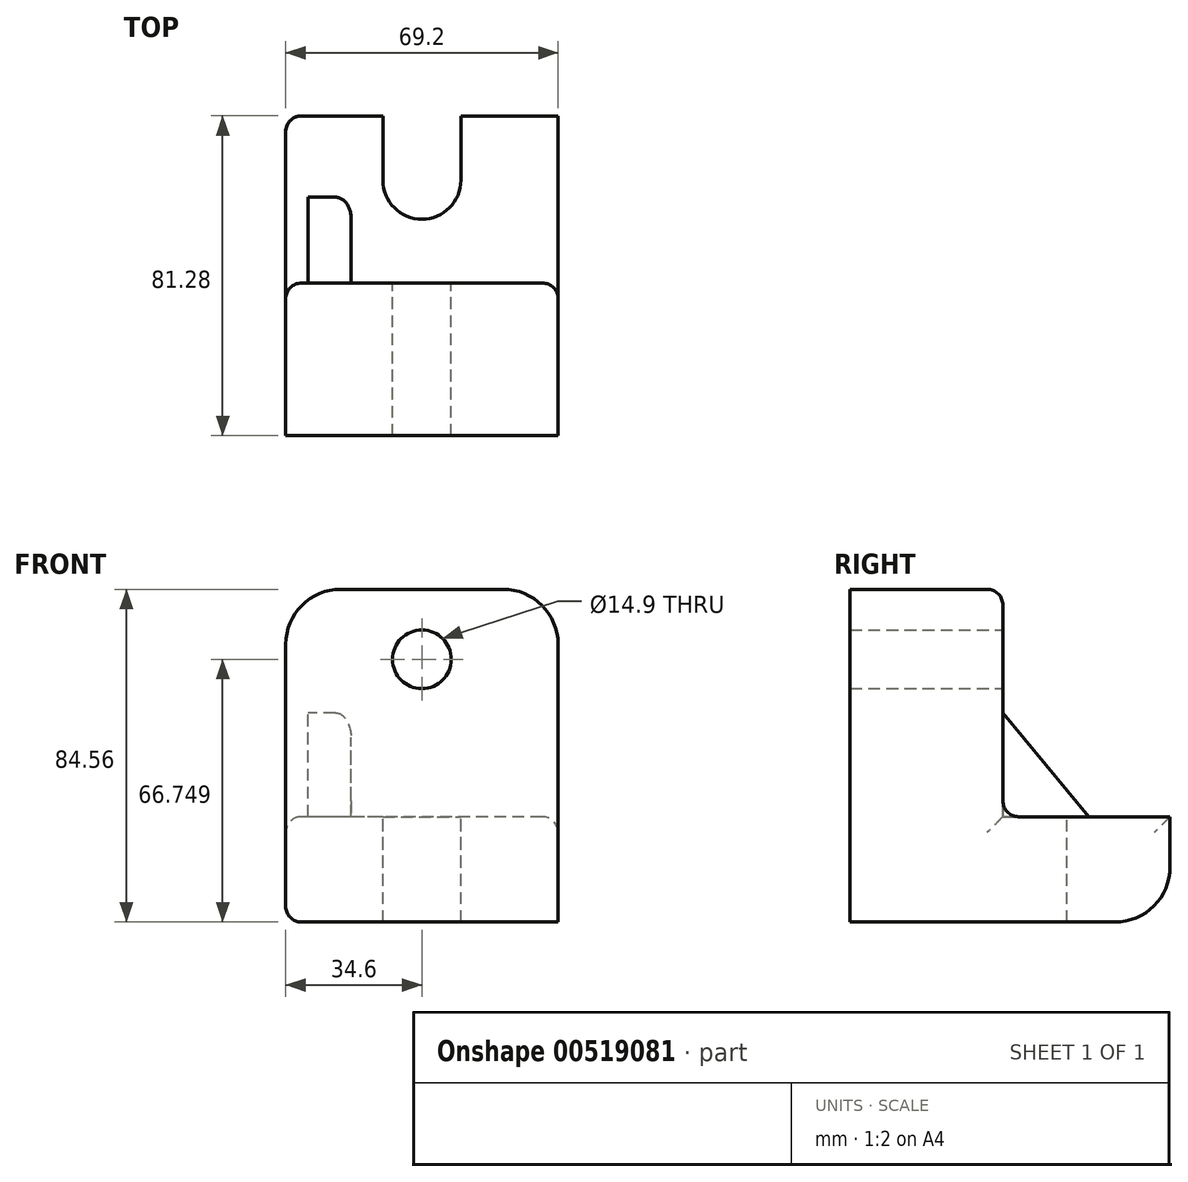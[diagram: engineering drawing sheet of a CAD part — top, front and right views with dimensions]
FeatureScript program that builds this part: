
annotation { "Feature Type Name" : "Feature", "Feature Type Description" : "" }
export const myFeature = defineFeature(function(context is Context, id is Id, definition is map)
    precondition{}
    {
        {
            var Q0;
            Q0=qCreatedBy(makeId("Right.planeOp"),FACE);
            var sketch = newSketch(context, id + "F0", { "sketchPlane" : qUnion([Q0])});
            skLineSegment(sketch, "E0.bottom", {"start": v(-19.4, 42.28) * mm, "end": v(19.4, 42.28) * mm});
            skLineSegment(sketch, "E0.top", {"start": v(-19.4, -42.28) * mm, "end": v(19.4, -42.28) * mm});
            skLineSegment(sketch, "E0.left", {"start": v(-19.4, 42.28) * mm, "end": v(-19.4, -42.28) * mm});
            skLineSegment(sketch, "E0.right", {"start": v(19.4, 42.28) * mm, "end": v(19.4, -15.52) * mm});
            skPoint(sketch, "E0.middle", {"position": v(0, 0) * mm});
            skLineSegment(sketch, "E1.bottom", {"start": v(-19.4, -42.28) * mm, "end": v(61.88, -42.28) * mm});
            skLineSegment(sketch, "E1.top", {"start": v(19.4, -15.52) * mm, "end": v(61.88, -15.52) * mm});
            skLineSegment(sketch, "E1.left", {"start": v(-19.4, -42.28) * mm, "end": v(-19.4, -15.52) * mm});
            skLineSegment(sketch, "E1.right", {"start": v(61.88, -42.28) * mm, "end": v(61.88, -15.52) * mm});
            skSolve(sketch);
        }
        {
            var Q0;
            Q0=makeQuery(id+"F0.imprint","IMPRINT",FACE,{"disambiguationData":[TD([[makeQuery(id+"F0.imprint","IMPRINT",EDGE,{"derivedFrom":sQuery(id+"F0.wireOp",EDGE,"E0.bottom")}),-1.0]])]});
            extrude(context, id + "F1", {"entities" : qUnion([Q0]), "endBound" : BoundingType.SYMMETRIC, "depth" : 69.2 * mm, "offsetDistance" : 25 * mm});
        }
        {
            var Q0;
            Q0=makeQuery(id+"F1.opExtrude","SWEPT_FACE",FACE,{"disambiguationData":[OSD([sQuery(id+"F0.wireOp",EDGE,"E1.top")])]});
            var sketch = newSketch(context, id + "F2", { "sketchPlane" : qUnion([Q0])});
            skCircle(sketch, "E2", {"center": v(0, 45.53) * mm, "radius": 9.91 * mm});
            skLineSegment(sketch, "E3", {"start": v(9.91, 45.53) * mm, "end": v(9.91, 61.88) * mm});
            skLineSegment(sketch, "E4", {"start": v(-9.91, 45.53) * mm, "end": v(-9.91, 61.88) * mm});
            skLineSegment(sketch, "E5", {"start": v(9.91, 61.88) * mm, "end": v(-9.91, 61.88) * mm});
            skSolve(sketch);
        }
        {
            var Q0;
            {var subQ0=sQuery(id+"F2.wireOp",EDGE,"E2");var subQ1=makeQuery(id+"F2.imprint","INTERSECT",VERTEX,{"derivedFrom":[subQ0,sQuery(id+"F2.wireOp",EDGE,"E3")]});Q0=makeQuery(id+"F2.imprint","IMPRINT",FACE,{"disambiguationData":[TD([[makeQuery(id+"F2.imprint","IMPRINT",EDGE,{"disambiguationData":[TD([[subQ1,-1.0]])],"derivedFrom":subQ0}),1.0]])]});}
            var Q1;
            {var subQ0=sQuery(id+"F2.wireOp",EDGE,"E3");Q1=makeQuery(id+"F2.imprint","IMPRINT",FACE,{"disambiguationData":[TD([[makeQuery(id+"F2.imprint","IMPRINT",EDGE,{"derivedFrom":subQ0}),1.0]])]});}
            extrude(context, id + "F3", {"entities" : qUnion([Q0, Q1]), "operationType" : NewBodyOperationType.REMOVE, "oppositeDirection" : true, "depth" : 85.7 * mm, "offsetDistance" : 25 * mm});
        }
        {
            var Q0;
            Q0=makeQuery(id+"F1.opExtrude","SWEPT_FACE",FACE,{"disambiguationData":[OSD([sQuery(id+"F0.wireOp",EDGE,"E0.right")])]});
            var sketch = newSketch(context, id + "F4", { "sketchPlane" : qUnion([Q0])});
            skCircle(sketch, "E6", {"center": v(0, 24.47) * mm, "radius": 7.45 * mm});
            skSolve(sketch);
        }
        {
            var Q0;
            Q0=makeQuery(id+"F4.imprint","IMPRINT",FACE,{"disambiguationData":[TD([[makeQuery(id+"F4.imprint","IMPRINT",EDGE,{"derivedFrom":sQuery(id+"F4.wireOp",EDGE,"E6")}),1.0]])]});
            extrude(context, id + "F5", {"entities" : qUnion([Q0]), "operationType" : NewBodyOperationType.REMOVE, "oppositeDirection" : true, "depth" : 63.3 * mm, "offsetDistance" : 25 * mm});
        }
        {
            var Q0;
            Q0=makeQuery(id+"F1.opExtrude","SWEPT_FACE",FACE,{"disambiguationData":[OSD([sQuery(id+"F0.wireOp",EDGE,"E0.right")])]});
            var sketch = newSketch(context, id + "F6", { "sketchPlane" : qUnion([Q0])});
            skLineSegment(sketch, "E7.bottom", {"start": v(18, -15.52) * mm, "end": v(28.86, -15.52) * mm});
            skLineSegment(sketch, "E7.top", {"start": v(18, 10.9) * mm, "end": v(28.86, 10.9) * mm});
            skLineSegment(sketch, "E7.left", {"start": v(18, -15.52) * mm, "end": v(18, 10.9) * mm});
            skLineSegment(sketch, "E7.right", {"start": v(28.86, -15.52) * mm, "end": v(28.86, 10.9) * mm});
            skSolve(sketch);
        }
        {
            var Q0;
            Q0=makeQuery(id+"F6.imprint","IMPRINT",FACE,{"disambiguationData":[TD([[makeQuery(id+"F6.imprint","IMPRINT",EDGE,{"derivedFrom":sQuery(id+"F6.wireOp",EDGE,"E7.bottom")}),1.0]])]});
            extrude(context, id + "F7", {"entities" : qUnion([Q0]), "operationType" : NewBodyOperationType.ADD, "depth" : 21.8 * mm, "offsetDistance" : 25 * mm});
        }
        {
            var Q0;
            Q0=makeQuery(id+"F7.opExtrude","SWEPT_FACE",FACE,{"disambiguationData":[OSD([sQuery(id+"F6.wireOp",EDGE,"E7.right")])]});
            var sketch = newSketch(context, id + "F8", { "sketchPlane" : qUnion([Q0])});
            skLineSegment(sketch, "E8", {"start": v(-19.4, 10.9) * mm, "end": v(-41.2, -15.52) * mm});
            skSolve(sketch);
        }
        {
            var Q0;
            Q0=makeQuery(id+"F8.imprint","IMPRINT",FACE,{"disambiguationData":[TD([[makeQuery(id+"F8.imprint","IMPRINT",EDGE,{"derivedFrom":sQuery(id+"F8.wireOp",EDGE,"E8")}),-1.0]])]});
            extrude(context, id + "F9", {"entities" : qUnion([Q0]), "operationType" : NewBodyOperationType.REMOVE, "oppositeDirection" : true, "depth" : 98.4 * mm, "offsetDistance" : 25 * mm});
        }
        {
            var Q0;
            Q0=makeQuery(id+"F1.opExtrude","CAP_EDGE",EDGE,{"disambiguationData":[OSD([sQuery(id+"F0.wireOp",EDGE,"E0.bottom")])],"isStart":true});
            var Q1;
            Q1=makeQuery(id+"F1.opExtrude","CAP_EDGE",EDGE,{"disambiguationData":[OSD([sQuery(id+"F0.wireOp",EDGE,"E0.bottom")])],"isStart":false});
            var Q2;
            Q2=makeQuery(id+"F1.opExtrude","SWEPT_EDGE",EDGE,{"disambiguationData":[OSD([sQuery(id+"F0.wireOp",EDGE,"E1.bottom"),sQuery(id+"F0.wireOp",EDGE,"E1.left")])]});
            fillet(context, id + "F10", {"entities" : qUnion([Q0, Q1, Q2]), "radius" : 14 * mm, "tangentPropagation" : true, "allowEdgeOverflow" : false});
        }
        {
            var Q0;
            Q0=makeQuery(id+"F1.opExtrude","CAP_EDGE",EDGE,{"disambiguationData":[OSD([sQuery(id+"F0.wireOp",EDGE,"E1.top")])],"isStart":true});
            var Q1;
            Q1=makeQuery(id+"F1.opExtrude","CAP_EDGE",EDGE,{"disambiguationData":[OSD([sQuery(id+"F0.wireOp",EDGE,"E0.right")])],"isStart":true});
            var Q2;
            Q2=makeQuery(id+"F1.opExtrude","CAP_EDGE",EDGE,{"disambiguationData":[OSD([sQuery(id+"F0.wireOp",EDGE,"E1.top")])],"isStart":false});
            var Q3;
            Q3=makeQuery(id+"F1.opExtrude","CAP_EDGE",EDGE,{"disambiguationData":[OSD([sQuery(id+"F0.wireOp",EDGE,"E1.bottom")])],"isStart":true});
            var Q4;
            Q4=makeQuery(id+"F9.boolean.opBoolean","COPY",EDGE,{"derivedFrom":makeQuery(id+"F9.opExtrude","CAP_EDGE",EDGE,{"disambiguationData":[OSD([sQuery(id+"F8.wireOp",EDGE,"E8")])],"isStart":true})});
            var Q5;
            Q5=makeQuery(id+"F9.boolean.opBoolean","INTERSECT",EDGE,{"derivedFrom":[makeQuery(id+"F7.opExtrude","SWEPT_FACE",FACE,{"disambiguationData":[OSD([sQuery(id+"F6.wireOp",EDGE,"E7.left")])]}),makeQuery(id+"F9.opExtrude","SWEPT_FACE",FACE,{"disambiguationData":[OSD([sQuery(id+"F8.wireOp",EDGE,"E8")])]})]});
            var Q6;
            Q6=makeQuery(id+"F9PlTN49vfgT7nn_1.1.F9.boolean.opBoolean","INTERSECT",EDGE,{"derivedFrom":[makeQuery(id+"F9PlTN49vfgT7nn_1.1.F7.opExtrude","SWEPT_FACE",FACE,{"disambiguationData":[OSD([sQuery(id+"F6.wireOp",EDGE,"E7.left")])]}),makeQuery(id+"F9PlTN49vfgT7nn_1.1.F9.opExtrude","SWEPT_FACE",FACE,{"disambiguationData":[OSD([sQuery(id+"F8.wireOp",EDGE,"E8")])]})]});
            var Q7;
            Q7=makeQuery(id+"F9PlTN49vfgT7nn_1.1.F9.boolean.opBoolean","COPY",EDGE,{"derivedFrom":makeQuery(id+"F9PlTN49vfgT7nn_1.1.F9.opExtrude","CAP_EDGE",EDGE,{"disambiguationData":[OSD([sQuery(id+"F8.wireOp",EDGE,"E8")])],"isStart":true})});
            var Q8;
            {var subQ0=sQuery(id+"F0.wireOp",EDGE,"E0.right");var subQ2=sQuery(id+"F0.wireOp",EDGE,"E1.top");var subQ4=sQuery(id+"F6.wireOp",EDGE,"E7.left");var subQ5=makeQuery(id+"F7.opExtrude","SWEPT_FACE",FACE,{"disambiguationData":[OSD([subQ4])]});Q8=makeQuery(id+"F9PlTN49vfgT7nn_1.1.F7.boolean.opBoolean","SPLIT",EDGE,{"disambiguationData":[TD([subQ5])],"derivedFrom":makeQuery(id+"F7.boolean.opBoolean","SPLIT",EDGE,{"disambiguationData":[TD([subQ5])],"derivedFrom":makeQuery(id+"F1.opExtrude","SWEPT_EDGE",EDGE,{"disambiguationData":[OSD([subQ0,subQ2])]})})});}
            fillet(context, id + "F11", {"entities" : qUnion([Q0, Q1, Q2, Q3, Q4, Q5, Q6, Q7, Q8]), "radius" : 4 * mm, "tangentPropagation" : true, "allowEdgeOverflow" : false});
        }
    });
